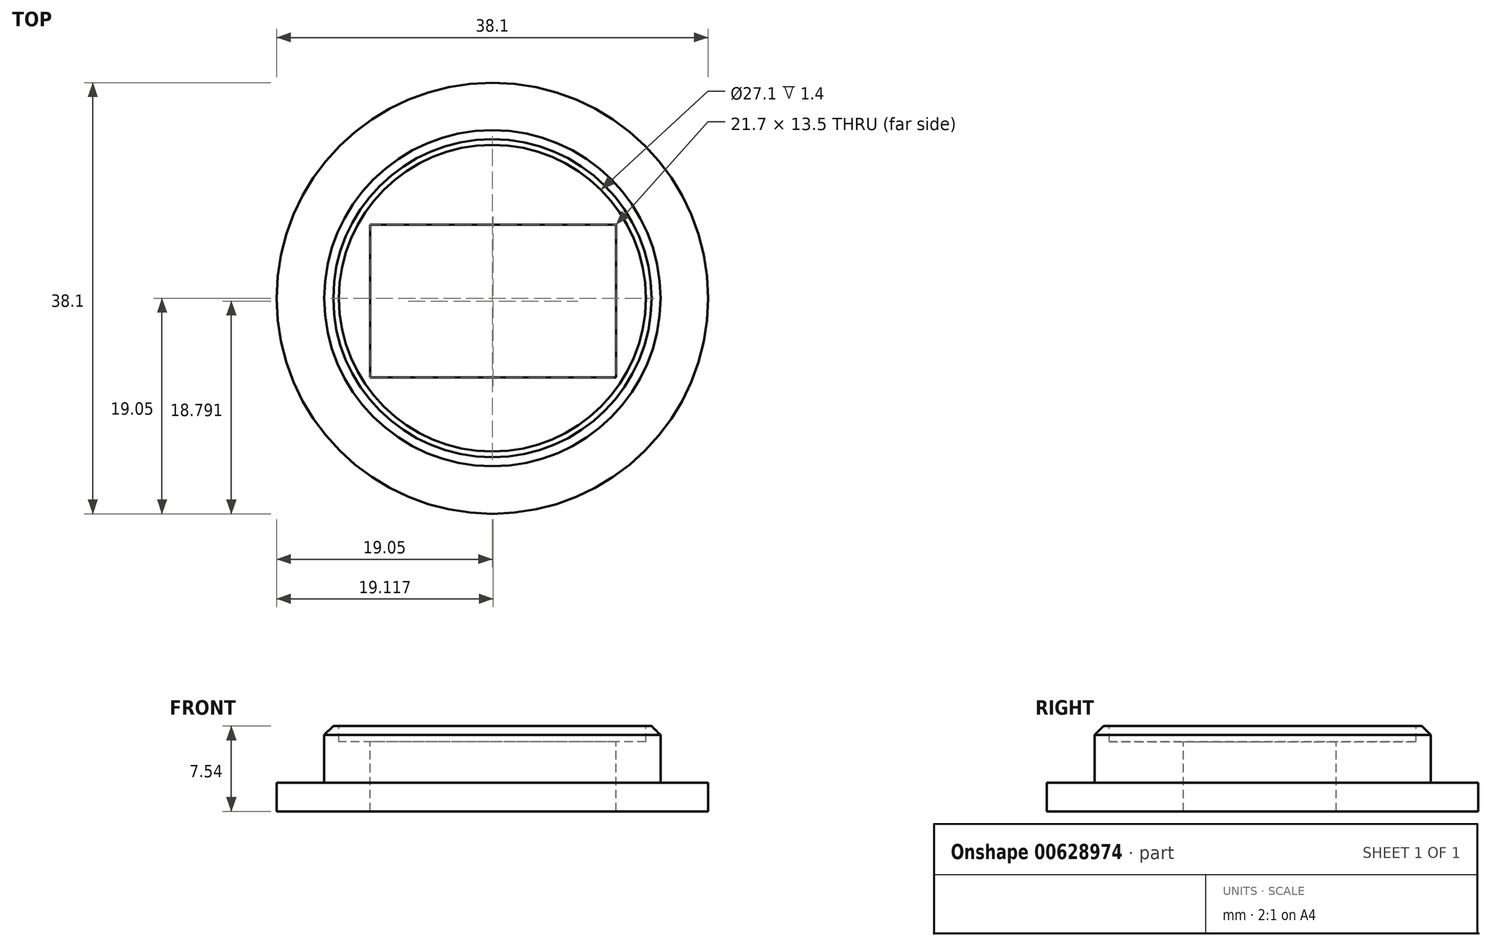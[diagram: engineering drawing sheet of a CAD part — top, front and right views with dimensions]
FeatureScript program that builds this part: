
annotation { "Feature Type Name" : "Feature", "Feature Type Description" : "" }
export const myFeature = defineFeature(function(context is Context, id is Id, definition is map)
    precondition{}
    {
        {
            var Q0;
            Q0=qCreatedBy(makeId("Top.planeOp"),FACE);
            var sketch = newSketch(context, id + "F0", { "sketchPlane" : qUnion([Q0])});
            skCircle(sketch, "E0", {"center": v(0, 0) * mm, "radius": 19.05 * mm});
            skSolve(sketch);
        }
        {
            var Q0;
            Q0 = qSketchRegion(id + "F0", true);
            extrude(context, id + "F1", {"entities" : qUnion([Q0]), "depth" : 2.54 * mm, "offsetDistance" : 25 * mm});
        }
        {
            var Q0;
            Q0=makeQuery(id+"F1.opExtrude","CAP_FACE",FACE,{"disambiguationData":[OSD([sQuery(id+"F0.wireOp",EDGE,"E0")])],"isStart":false});
            var sketch = newSketch(context, id + "F2", { "sketchPlane" : qUnion([Q0])});
            skCircle(sketch, "E1", {"center": v(0, 0) * mm, "radius": 14.85 * mm});
            skSolve(sketch);
        }
        {
            var Q0;
            Q0=makeQuery(id+"F2.imprint","IMPRINT",FACE,{"disambiguationData":[TD([[makeQuery(id+"F2.imprint","IMPRINT",EDGE,{"derivedFrom":sQuery(id+"F2.wireOp",EDGE,"E1")}),1.0]])]});
            extrude(context, id + "F3", {"entities" : qUnion([Q0]), "operationType" : NewBodyOperationType.ADD, "depth" : 5 * mm, "offsetDistance" : 25 * mm});
        }
        {
            var Q0;
            Q0=makeQuery(id+"F3.opExtrude","CAP_FACE",FACE,{"disambiguationData":[OSD([sQuery(id+"F2.wireOp",EDGE,"E1")])],"isStart":false});
            var sketch = newSketch(context, id + "F4", { "sketchPlane" : qUnion([Q0])});
            skLineSegment(sketch, "E2.bottom", {"start": v(-10.78, 6.5) * mm, "end": v(10.92, 6.5) * mm});
            skLineSegment(sketch, "E2.top", {"start": v(-10.78, -7) * mm, "end": v(10.92, -7) * mm});
            skLineSegment(sketch, "E2.left", {"start": v(-10.78, 6.5) * mm, "end": v(-10.78, -7) * mm});
            skLineSegment(sketch, "E2.right", {"start": v(10.92, 6.5) * mm, "end": v(10.92, -7) * mm});
            skSolve(sketch);
        }
        {
            var Q0;
            Q0=makeQuery(id+"F4.imprint","IMPRINT",FACE,{"disambiguationData":[TD([[makeQuery(id+"F4.imprint","IMPRINT",EDGE,{"derivedFrom":sQuery(id+"F4.wireOp",EDGE,"E2.bottom")}),-1.0]])]});
            extrude(context, id + "F5", {"entities" : qUnion([Q0]), "operationType" : NewBodyOperationType.REMOVE, "oppositeDirection" : true, "depth" : 10 * mm, "offsetDistance" : 25 * mm});
        }
        {
            var Q0;
            Q0=makeQuery(id+"F3.opExtrude","CAP_FACE",FACE,{"disambiguationData":[OSD([sQuery(id+"F2.wireOp",EDGE,"E1")])],"isStart":false});
            var sketch = newSketch(context, id + "F6", { "sketchPlane" : qUnion([Q0])});
            skCircle(sketch, "E3", {"center": v(0, 0) * mm, "radius": 13.55 * mm});
            skSolve(sketch);
        }
        {
            var Q0;
            Q0 = qSketchRegion(id + "F6", true);
            extrude(context, id + "F7", {"entities" : qUnion([Q0]), "operationType" : NewBodyOperationType.REMOVE, "oppositeDirection" : true, "depth" : 1.4 * mm, "offsetDistance" : 25 * mm});
        }
        {
            var Q0;
            Q0=makeQuery(id+"F3.opExtrude","CAP_EDGE",EDGE,{"disambiguationData":[OSD([sQuery(id+"F2.wireOp",EDGE,"E1")])],"isStart":false});
            chamfer(context, id + "F8", {"entities" : qUnion([Q0]), "width" : 0.8 * mm, "tangentPropagation" : true});
        }
    });
